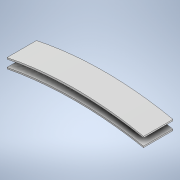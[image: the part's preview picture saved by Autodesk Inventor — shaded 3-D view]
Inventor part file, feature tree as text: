
AUTODESK INVENTOR PART (.ipt)
format: ipt  version: 2020.2 (Build 242310000, 310)  size: 113,152 bytes
history: native  units: mm
features: extrude x1, sketch x1
ambient origin geometry x8: Origin, YZ Plane, XZ Plane, XY Plane, X Axis, Y Axis, Z Axis, Center Point
bodies: Solide1 (feature_tree)
feature tree (2):
  extrude  "Extrusion1"  Depth=785.7mm
  sketch  "Esquisse1"
